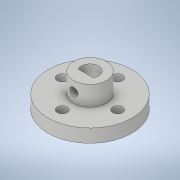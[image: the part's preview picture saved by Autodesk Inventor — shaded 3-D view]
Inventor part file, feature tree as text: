
AUTODESK INVENTOR PART (.ipt)
format: ipt  version: 2022 (Build 260153000, 153)  size: 158,208 bytes
history: native  units: mm
features: extrude x6, sketch x6, plane x1
ambient origin geometry x8: Origin, YZ Plane, XZ Plane, XY Plane, X Axis, Y Axis, Z Axis, Center Point
bodies: Solid1 (feature_tree)
feature tree (13):
  extrude  "Extrusion1"  Depth=4.0mm TaperAngle=0.0deg
  extrude  "Extrusion2"  Depth=8.0mm TaperAngle=0.0deg
  extrude  "Extrusion9"  Depth=2.0mm TaperAngle=0.0deg
  extrude  "Extrusion10"  Depth=10.0mm
  extrude  "Extrusion11"  Depth=1.3125mm
  plane  "Work Plane1"
  extrude  "Extrusion12"  Depth=10.0mm
  sketch  "Sketch1"  dims[d0=25.4mm d1=4.0mm d2=0.0mm]
  sketch  "Sketch2"  dims[d5=40.0mm d7=360.0deg d9=8.0mm d10=0.0mm]
  sketch  "Sketch10"  dims[d49=7.0mm d50=2.0mm d51=0.0mm]
  sketch  "Sketch11"  dims[d52=10.0mm d53=5.25mm]
  sketch  "Sketch12"  dims[d54=6.0mm d55=0.0mm d56=1.3125mm]
  sketch  "Sketch13"  dims[d57=6.0mm d58=0.0mm d60=2.5mm d61=10.0mm d62=0.0mm]
